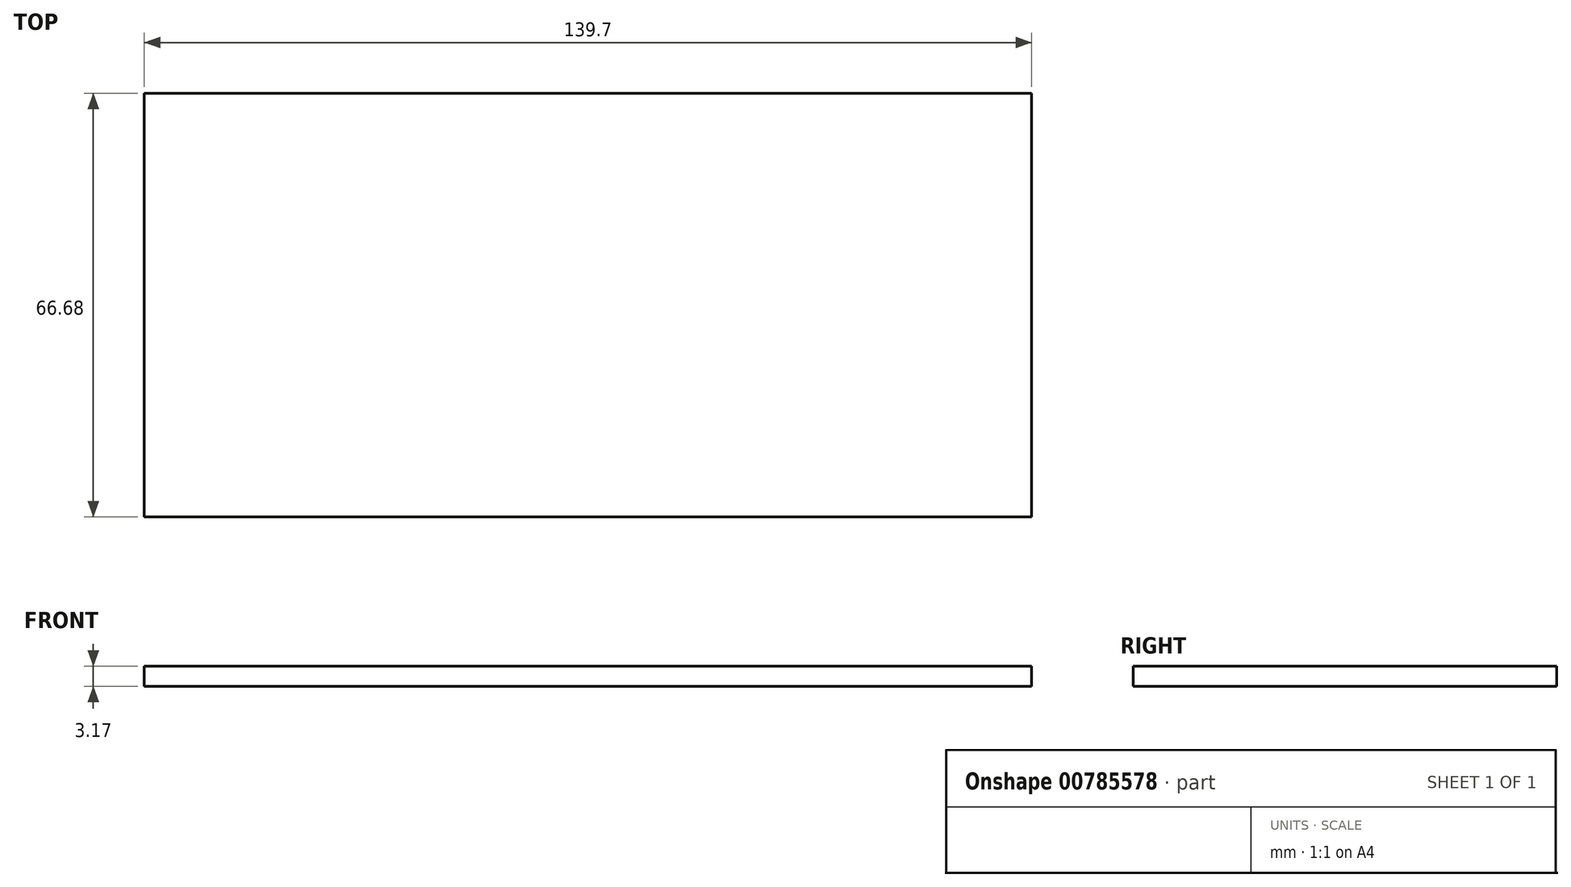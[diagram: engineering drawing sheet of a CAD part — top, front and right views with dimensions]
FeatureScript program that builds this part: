
annotation { "Feature Type Name" : "Feature", "Feature Type Description" : "" }
export const myFeature = defineFeature(function(context is Context, id is Id, definition is map)
    precondition{}
    {
        {
            var Q0;
            Q0=qCreatedBy(makeId("Top.planeOp"),FACE);
            var sketch = newSketch(context, id + "F0", { "sketchPlane" : qUnion([Q0])});
            skLineSegment(sketch, "E0.bottom", {"start": v(69.85, 33.34) * mm, "end": v(-69.85, 33.34) * mm});
            skLineSegment(sketch, "E0.top", {"start": v(69.85, -33.34) * mm, "end": v(-69.85, -33.34) * mm});
            skLineSegment(sketch, "E0.left", {"start": v(69.85, 33.34) * mm, "end": v(69.85, -33.34) * mm});
            skLineSegment(sketch, "E0.right", {"start": v(-69.85, 33.34) * mm, "end": v(-69.85, -33.34) * mm});
            skPoint(sketch, "E0.middle", {"position": v(0, 0) * mm});
            skSolve(sketch);
        }
        {
            var Q0;
            Q0=makeQuery(id+"F0.imprint","IMPRINT",FACE,{"disambiguationData":[TD([[makeQuery(id+"F0.imprint","IMPRINT",EDGE,{"derivedFrom":sQuery(id+"F0.wireOp",EDGE,"E0.bottom")}),1.0]])]});
            extrude(context, id + "F1", {"entities" : qUnion([Q0]), "depth" : 3.17 * mm, "offsetDistance" : 25.4 * mm});
        }
    });
